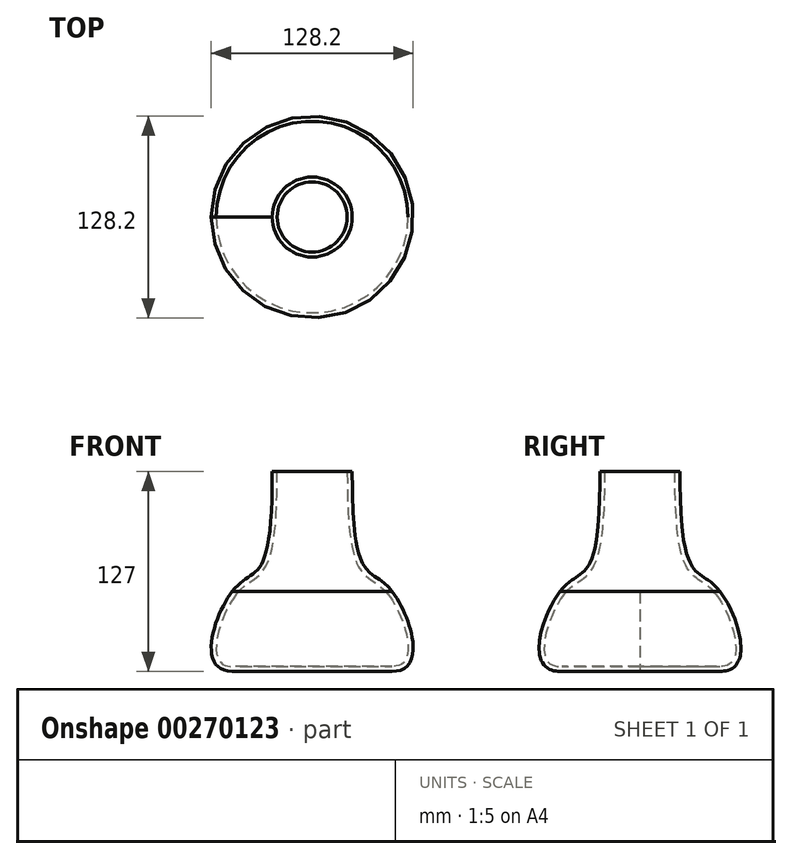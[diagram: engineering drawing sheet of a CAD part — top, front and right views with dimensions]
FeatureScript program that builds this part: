
annotation { "Feature Type Name" : "Feature", "Feature Type Description" : "" }
export const myFeature = defineFeature(function(context is Context, id is Id, definition is map)
    precondition{}
    {
        {
            var Q0;
            Q0=qCreatedBy(makeId("Front.planeOp"),FACE);
            var sketch = newSketch(context, id + "F0", { "sketchPlane" : qUnion([Q0])});
            skLineSegment(sketch, "E0.bottom", {"start": v(0, 0) * mm, "end": v(50.8, 0) * mm});
            skLineSegment(sketch, "E0.top", {"start": v(0, 50.8) * mm, "end": v(50.8, 50.8) * mm});
            skLineSegment(sketch, "E0.left", {"start": v(0, 0) * mm, "end": v(0, 50.8) * mm});
            skLineSegment(sketch, "E0.right", {"start": v(50.8, 0) * mm, "end": v(50.8, 50.8) * mm});
            skLineSegment(sketch, "E1", {"start": v(0, 50.8) * mm, "end": v(0, 127) * mm});
            skLineSegment(sketch, "E2", {"start": v(0, 127) * mm, "end": v(25.4, 127) * mm});
            skFitSpline(sketch, "E3", {"points": [v(25.4, 127) * mm, v(50.8, 50.8) * mm, v(50.8, 0) * mm], "startDerivative": vector(0, -410.4) * mm, "endDerivative": vector(-158.56, 0) * mm});
            skSolve(sketch);
        }
        {
            var Q0;
            Q0 = qSketchRegion(id + "F0", true);
            var Q1;
            Q1=sQuery(id+"F0.wireOp",EDGE,"E1");
            revolve(context, id + "F1", {"entities" : qUnion([Q0]), "axis" : qUnion([Q1]), "revolveType" : RevolveType.FULL});
        }
        {
            var Q0;
            Q0=makeQuery(id+"F1.opRevolve","SWEPT_FACE",FACE,{"disambiguationData":[OSD([sQuery(id+"F0.wireOp",EDGE,"E2")])]});
            shell(context, id + "F2", {"entities" : qUnion([Q0]), "thickness" : 3.17 * mm});
        }
    });
